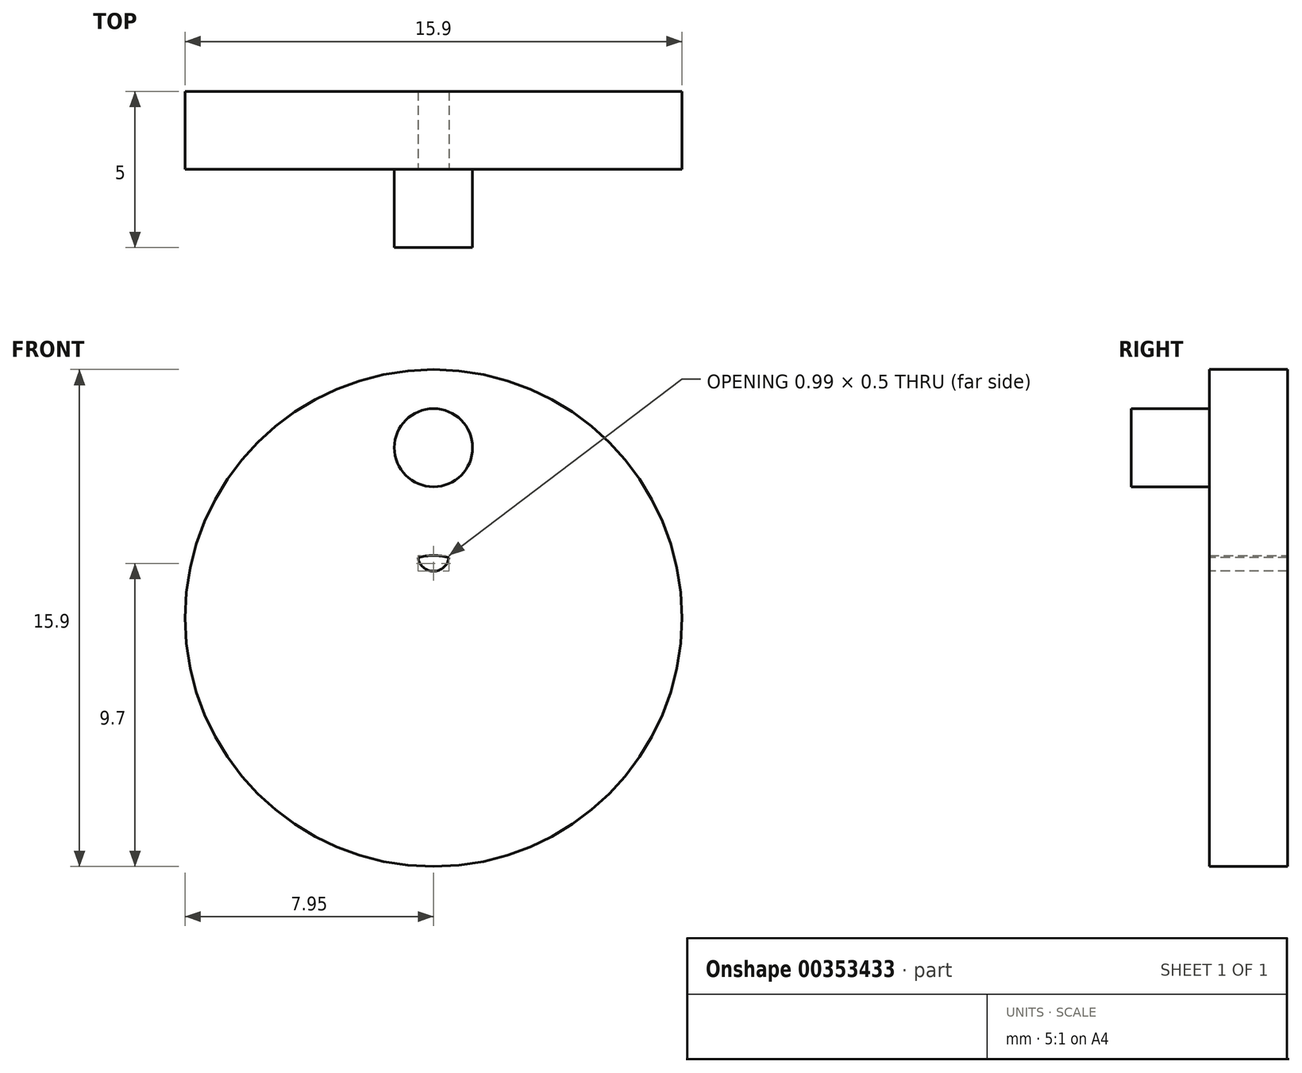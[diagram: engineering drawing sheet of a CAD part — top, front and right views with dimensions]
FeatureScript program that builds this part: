
annotation { "Feature Type Name" : "Feature", "Feature Type Description" : "" }
export const myFeature = defineFeature(function(context is Context, id is Id, definition is map)
    precondition{}
    {
        {
            var Q0;
            Q0=qCreatedBy(makeId("Front.planeOp"),FACE);
            var sketch = newSketch(context, id + "F0", { "sketchPlane" : qUnion([Q0])});
            skCircle(sketch, "E0", {"center": v(0, 0) * mm, "radius": 2 * mm});
            skCircle(sketch, "E1", {"center": v(0, 0) * mm, "radius": 7.95 * mm});
            skSolve(sketch);
        }
        {
            var Q0;
            Q0=makeQuery(id+"F0.imprint","IMPRINT",FACE,{"disambiguationData":[TD([[makeQuery(id+"F0.imprint","IMPRINT",EDGE,{"derivedFrom":sQuery(id+"F0.wireOp",EDGE,"E0")}),-1.0]])]});
            extrude(context, id + "F1", {"entities" : qUnion([Q0]), "depth" : 2.5 * mm});
        }
        {
            var Q0;
            Q0=makeQuery(id+"F1.opExtrude","CAP_FACE",FACE,{"disambiguationData":[OSD([sQuery(id+"F0.wireOp",EDGE,"E0"),sQuery(id+"F0.wireOp",EDGE,"E1")])],"isStart":false});
            var sketch = newSketch(context, id + "F2", { "sketchPlane" : qUnion([Q0])});
            skCircle(sketch, "E2", {"center": v(0, 5.45) * mm, "radius": 1.25 * mm});
            skCircle(sketch, "E3.0", {"center": v(0, 0) * mm, "radius": 7.95 * mm});
            skSolve(sketch);
        }
        {
            var Q0;
            Q0=makeQuery(id+"F2.imprint","IMPRINT",FACE,{"disambiguationData":[TD([[makeQuery(id+"F2.imprint","IMPRINT",EDGE,{"derivedFrom":sQuery(id+"F2.wireOp",EDGE,"E2")}),1.0]])]});
            extrude(context, id + "F3", {"entities" : qUnion([Q0]), "operationType" : NewBodyOperationType.ADD, "depth" : 2.5 * mm});
        }
        {
            var Q0;
            Q0=makeQuery(id+"F1.opExtrude","CAP_FACE",FACE,{"disambiguationData":[OSD([sQuery(id+"F0.wireOp",EDGE,"E0"),sQuery(id+"F0.wireOp",EDGE,"E1")])],"isStart":false});
            var sketch = newSketch(context, id + "F4", { "sketchPlane" : qUnion([Q0])});
            skCircle(sketch, "E4.0", {"center": v(0, 0) * mm, "radius": 2 * mm});
            skArc(sketch, "E5", {"start": v(0.5, 1.94) * mm, "mid": v(0, 1.5) * mm, "end": v(-0.5, 1.94) * mm});
            skSolve(sketch);
        }
        {
            var Q0;
            {var subQ0=sQuery(id+"F4.wireOp",EDGE,"E5");Q0=makeQuery(id+"F4.imprint","IMPRINT",FACE,{"disambiguationData":[TD([[makeQuery(id+"F4.imprint","IMPRINT",EDGE,{"derivedFrom":subQ0}),-1.0]])]});}
            var Q1;
            Q1=makeQuery(id+"F1.opExtrude","CAP_FACE",FACE,{"disambiguationData":[OSD([sQuery(id+"F0.wireOp",EDGE,"E0"),sQuery(id+"F0.wireOp",EDGE,"E1")])],"isStart":true});
            extrude(context, id + "F5", {"entities" : qUnion([Q0]), "operationType" : NewBodyOperationType.ADD, "endBound" : BoundingType.UP_TO_SURFACE, "oppositeDirection" : true, "endBoundEntityFace" : qUnion([Q1]), "depth" : 25 * mm});
        }
    });
